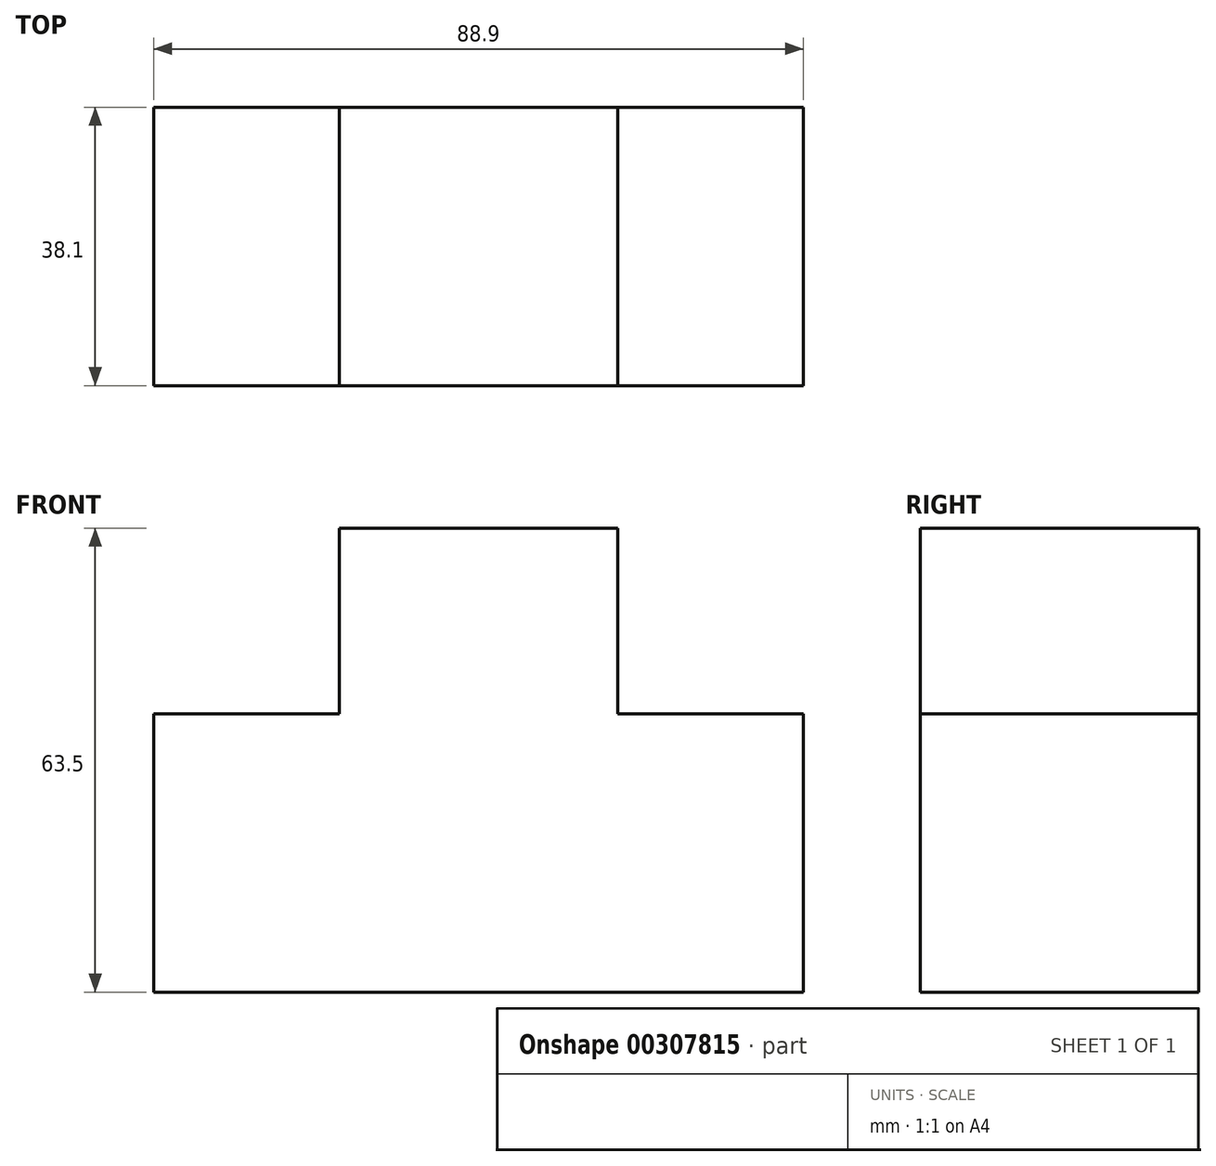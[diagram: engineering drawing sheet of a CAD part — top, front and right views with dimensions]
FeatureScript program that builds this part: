
annotation { "Feature Type Name" : "Feature", "Feature Type Description" : "" }
export const myFeature = defineFeature(function(context is Context, id is Id, definition is map)
    precondition{}
    {
        {
            var Q0;
            Q0=qCreatedBy(makeId("Front.planeOp"),FACE);
            var sketch = newSketch(context, id + "F0", { "sketchPlane" : qUnion([Q0])});
            skLineSegment(sketch, "E0", {"start": v(-41.33, -63.5) * mm, "end": v(47.57, -63.5) * mm});
            skLineSegment(sketch, "E1", {"start": v(-41.33, -63.5) * mm, "end": v(-41.33, -25.4) * mm});
            skLineSegment(sketch, "E2", {"start": v(-41.33, -25.4) * mm, "end": v(-15.93, -25.4) * mm});
            skLineSegment(sketch, "E3", {"start": v(-15.93, -25.4) * mm, "end": v(-15.93, 0) * mm});
            skLineSegment(sketch, "E4", {"start": v(-15.93, 0) * mm, "end": v(22.17, 0) * mm});
            skLineSegment(sketch, "E5", {"start": v(22.17, 0) * mm, "end": v(22.17, -25.4) * mm});
            skLineSegment(sketch, "E6", {"start": v(22.17, -25.4) * mm, "end": v(47.57, -25.4) * mm});
            skLineSegment(sketch, "E7", {"start": v(47.57, -25.4) * mm, "end": v(47.57, -63.5) * mm});
            skSolve(sketch);
        }
        {
            var Q0;
            Q0=makeQuery(id+"F0.imprint","IMPRINT",FACE,{"disambiguationData":[TD([[makeQuery(id+"F0.imprint","IMPRINT",EDGE,{"derivedFrom":sQuery(id+"F0.wireOp",EDGE,"E0")}),1.0]])]});
            extrude(context, id + "F1", {"entities" : qUnion([Q0]), "depth" : 38.1 * mm});
        }
    });
